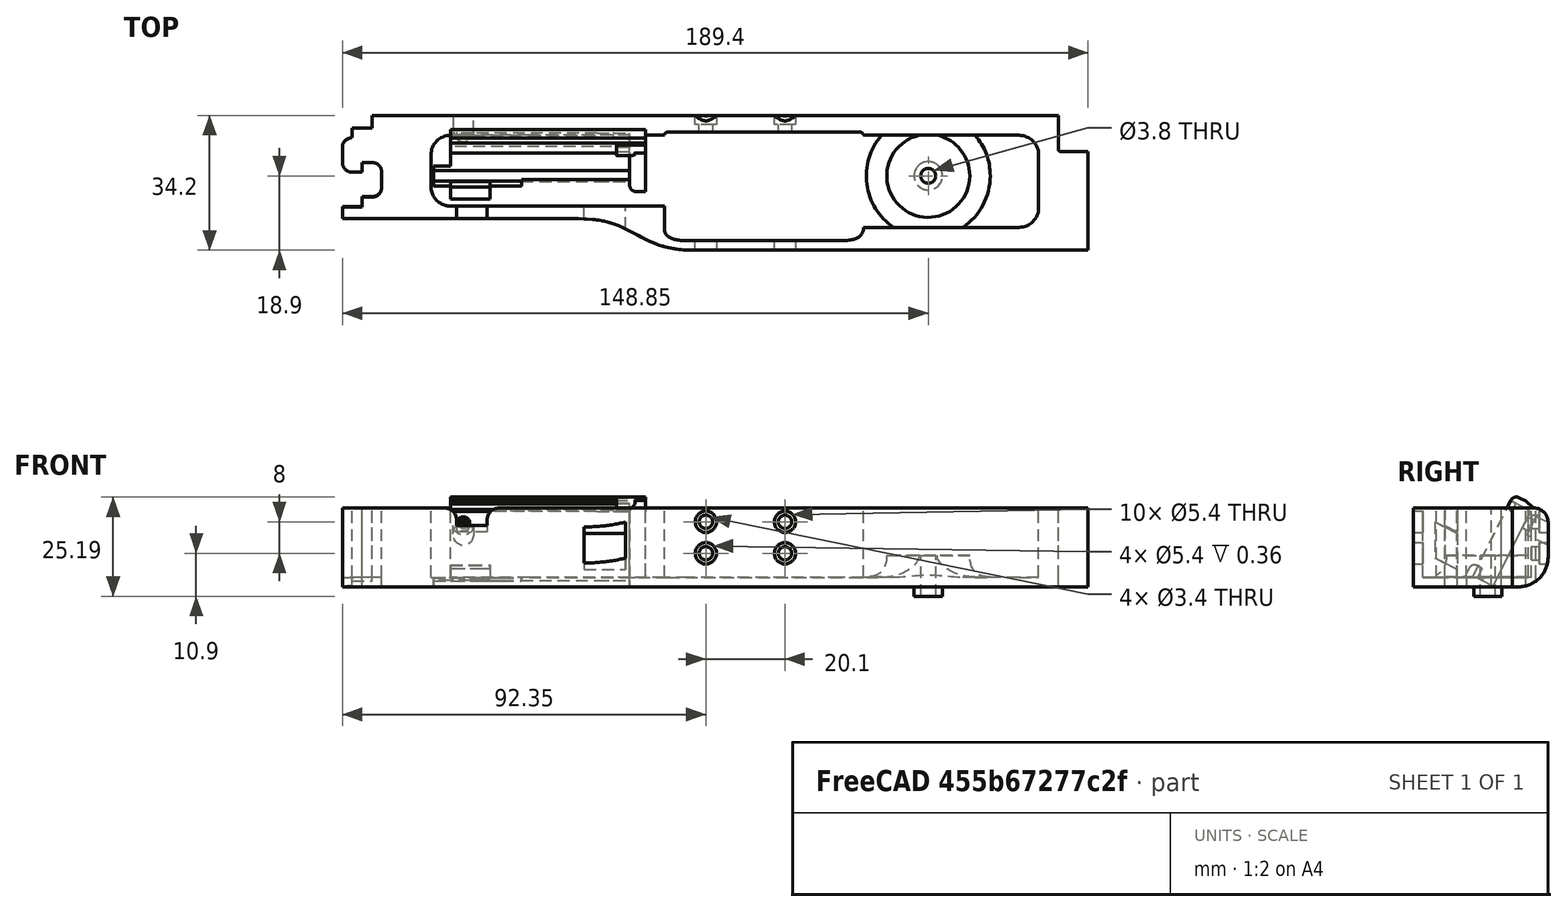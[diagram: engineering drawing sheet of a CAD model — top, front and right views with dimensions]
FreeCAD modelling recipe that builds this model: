
FCSTD DOCUMENT  (FreeCAD 0.19R0.19.2)
Label: v0_992
License: All rights reserved
LicenseURL: http://en.wikipedia.org/wiki/All_rights_reserved
objects: Sketcher::SketchObject×34, Part::Extrusion×28, Part::Cut×14, Part::Fillet×13, Part::MultiFuse×10, Part::Box×8, App::MeasureDistance×4, Part::Revolution×1, Mesh::Feature×1
note: 108 computed .brp shape members not serialized (recipe doc carries the construction recipe); baked Part::Feature solids carry a one-line shape summary decoded from their .brp

FEATURE [Sketcher::SketchObject] Sketch
  FullyConstrained = true
  sketch-geometry (36):
    g0: LineSegment StartX=0 StartY=0 StartZ=0 EndX=154.4 EndY=0 EndZ=0
    g1: LineSegment StartX=154.4 StartY=0 StartZ=0 EndX=154.4 EndY=-7.6 EndZ=0
    g2: LineSegment StartX=32.5209 StartY=-26.2 StartZ=0 EndX=-7.5 EndY=-26.2 EndZ=0
    g3-g7: Circle x5 (B-spline internal-alignment scaffolding for g8; pole/knot coordinates omitted)
    g8: BSplineCurve PolesCount=5 KnotsCount=3 Degree=3 IsPeriodic=0
    g9: GeomPoint X=61.85 Y=-33.8 Z=0
    g10: GeomPoint X=47.185 Y=-29.9 Z=0
    g11: GeomPoint X=32.5209 Y=-26.2 Z=0
    g12: Circle CenterX=121.35 CenterY=-14.3 CenterZ=0 NormalX=0 NormalY=0 NormalZ=1 AngleXU=0 Radius=3.25
    g13: LineSegment StartX=-7.5 StartY=-26.2 StartZ=0 EndX=-27.5 EndY=-26.2 EndZ=0
    g14: LineSegment StartX=-20 StartY=0 StartZ=0 EndX=0 EndY=0 EndZ=0
    g15: LineSegment StartX=-25 StartY=-3.1 StartZ=0 EndX=-20 EndY=-3.1 EndZ=0
    g16: LineSegment StartX=-25 StartY=-3.1 StartZ=0 EndX=-25 EndY=-5.6 EndZ=0
    g17: LineSegment StartX=-27.5 StartY=-8.1 StartZ=0 EndX=-27.5 EndY=-11.85 EndZ=0
    g18: ArcOfCircle CenterX=-25 CenterY=-8.1 CenterZ=0 NormalX=0 NormalY=0 NormalZ=1 AngleXU=0 Radius=2.5 StartAngle=1.5708 EndAngle=3.14159
    g19: LineSegment StartX=-25 StartY=-14.35 StartZ=0 EndX=-22.5 EndY=-14.35 EndZ=0
    g20: ArcOfCircle CenterX=-25 CenterY=-11.85 CenterZ=0 NormalX=0 NormalY=0 NormalZ=1 AngleXU=0 Radius=2.5 StartAngle=3.14159 EndAngle=4.71239
    g21: LineSegment StartX=-22.5 StartY=-14.35 StartZ=0 EndX=-22.5 EndY=-11.85 EndZ=0
    g22: LineSegment StartX=-22.5 StartY=-11.85 StartZ=0 EndX=-20 EndY=-11.85 EndZ=0
    g23: ArcOfCircle CenterX=-20 CenterY=-14.35 CenterZ=0 NormalX=0 NormalY=0 NormalZ=1 AngleXU=0 Radius=2.5 StartAngle=8e-16 EndAngle=1.5708
    g24: LineSegment StartX=-17.5 StartY=-14.35 StartZ=0 EndX=-17.5 EndY=-18.1 EndZ=0
    g25: ArcOfCircle CenterX=-20 CenterY=-18.1 CenterZ=0 NormalX=0 NormalY=0 NormalZ=1 AngleXU=0 Radius=2.5 StartAngle=4.71239 EndAngle=6.28319
    g26: LineSegment StartX=-22.5 StartY=-20.6 StartZ=0 EndX=-20 EndY=-20.6 EndZ=0
    g27: LineSegment StartX=-22.5 StartY=-20.6 StartZ=0 EndX=-22.5 EndY=-23.1 EndZ=0
    g28: LineSegment StartX=-27.5 StartY=-23.1 StartZ=0 EndX=-22.5 EndY=-23.1 EndZ=0
    g29: LineSegment StartX=-20 StartY=-3.1 StartZ=0 EndX=-20 EndY=0 EndZ=0
    g30: LineSegment StartX=-27.5 StartY=-23.1 StartZ=0 EndX=-27.5 EndY=-26.2 EndZ=0
    g31: LineSegment StartX=154.4 StartY=-7.6 StartZ=0 EndX=154.4 EndY=-8.6 EndZ=0
    g32: ArcOfCircle CenterX=154.9 CenterY=-8.6 CenterZ=0 NormalX=0 NormalY=0 NormalZ=1 AngleXU=0 Radius=0.5 StartAngle=3.14159 EndAngle=4.71239
    g33: LineSegment StartX=154.9 StartY=-9.1 StartZ=0 EndX=161.9 EndY=-9.1 EndZ=0
    g34: LineSegment StartX=161.9 StartY=-9.1 StartZ=0 EndX=161.9 EndY=-33.8 EndZ=0
    g35: LineSegment StartX=161.9 StartY=-33.8 StartZ=0 EndX=61.85 EndY=-33.8 EndZ=0
  constraints (72):
    c: PointOnObject(g0,g-2)
    c: Horizontal(g0)
    c: Distance(g0) = 154.4
    c: DistanceY(g-1,g0) = 0
    c: Vertical(g1)
    c: Distance(g1) = 7.6
    c: Coincident(g1,g0)
    c: Horizontal(g2)
    c: Block(g2)
    c: Weight(g3) = 1
    c: Coincident(g8,g2)
    c: InternalAlignment(g3-g7 -> g8) x5
    c: InternalAlignment(g9,g8)
    c: InternalAlignment(g10,g8)
    c: InternalAlignment(g11,g8)
    c: Block(g12)
    c: Coincident(g13,g2)
    c: Horizontal(g13)
    c: Distance(g13) = 20
    c: Horizontal(g14)
    c: Distance(g14) = 20
    c: Coincident(g14,g0)
    c: Horizontal(g15)
    c: Vertical(g16)
    c: Coincident(g16,g15)
    c: Vertical(g17)
    c: Coincident(g18,g16)
    c: Block(g18)
    c: Coincident(g17,g18)
    c: Horizontal(g19)
    c: Coincident(g20,g17)
    c: Block(g20)
    c: Block(g19)
    c: Vertical(g21)
    c: Coincident(g21,g19)
    c: Horizontal(g22)
    c: Coincident(g22,g21)
    c: Coincident(g23,g22)
    c: Vertical(g24)
    c: Block(g23)
    c: Coincident(g24,g23)
    c: Coincident(g25,g24)
    c: Block(g25)
    c: Horizontal(g26)
    c: Coincident(g26,g25)
    c: Vertical(g27)
    c: Coincident(g27,g26)
    c: Horizontal(g28)
    c: Coincident(g28,g27)
    c: Block(g15)
    c: Block(g28)
    c: Coincident(g29,g15)
    c: Coincident(g29,g14)
    c: Vertical(g29)
    c: Coincident(g30,g28)
    c: Coincident(g30,g13)
    c: Vertical(g30)
    c: Vertical(g31)
    c: Distance(g31) = 1
    c: Coincident(g31,g1)
    c: Coincident(g32,g31)
    c: Block(g32)
    c: Coincident(g33,g32)
    c: Horizontal(g33)
    c: Coincident(g34,g33)
    c: Vertical(g34)
    c: Block(g34)
    c: Coincident(g35,g34)
    c: Horizontal(g35)
    c: Block(g35)
    c: Coincident(g8,g35)
    c: Block(g8)
FEATURE [Part::Extrusion] Extrude  label="mainBodyBaseExtrude"
  Base = -> Sketch
  Dir = (0,0,1)
  DirMode = 2
  FaceMakerClass = Part::FaceMakerBullseye
  LengthFwd = 2.4
  LengthRev = 0
  Solid = true
  Symmetric = false
FEATURE [Sketcher::SketchObject] Sketch001
  FullyConstrained = true
  sketch-geometry (75):
    g0: ArcOfCircle CenterX=144.4 CenterY=-10 CenterZ=0 NormalX=0 NormalY=0 NormalZ=1 AngleXU=0 Radius=5 StartAngle=4.345e-13 EndAngle=1.5708
    g1: LineSegment StartX=32.5209 StartY=-26.2 StartZ=0 EndX=-7.49911 EndY=-26.2 EndZ=0
    g2: LineSegment StartX=0 StartY=0 StartZ=0 EndX=154.4 EndY=0 EndZ=0
    g3-g7: Circle x5 (B-spline internal-alignment scaffolding for g8; pole/knot coordinates omitted)
    g8: BSplineCurve PolesCount=5 KnotsCount=3 Degree=3 IsPeriodic=0
    g9: GeomPoint X=61.85 Y=-33.8 Z=0
    g10: GeomPoint X=47.1857 Y=-29.9 Z=0
    g11: GeomPoint X=32.5209 Y=-26.2 Z=0
    g12: LineSegment StartX=154.4 StartY=0 StartZ=0 EndX=154.4 EndY=-7.6 EndZ=0
    g13: LineSegment StartX=20 StartY=-5 StartZ=0 EndX=54.35 EndY=-5 EndZ=0
    g14: LineSegment StartX=104.85 StartY=-5 StartZ=0 EndX=144.4 EndY=-5 EndZ=0
    g15: LineSegment StartX=54.35 StartY=-23 StartZ=0 EndX=20 EndY=-23 EndZ=0
    g16: LineSegment StartX=-27.4991 StartY=-26.2 StartZ=0 EndX=-7.49911 EndY=-26.2 EndZ=0
    g17: LineSegment StartX=-20 StartY=0 StartZ=0 EndX=0 EndY=0 EndZ=0
    g18: LineSegment StartX=-27.4991 StartY=-23.2 StartZ=0 EndX=-22.5 EndY=-23.2 EndZ=0
    g19: LineSegment StartX=-22.5 StartY=-20.7 StartZ=0 EndX=-22.5 EndY=-23.2 EndZ=0
    g20: LineSegment StartX=-22.5 StartY=-20.7 StartZ=0 EndX=-20 EndY=-20.7 EndZ=0
    g21: ArcOfCircle CenterX=-20 CenterY=-18.2 CenterZ=0 NormalX=0 NormalY=0 NormalZ=1 AngleXU=0 Radius=2.5 StartAngle=4.71239 EndAngle=6.28319
    g22: LineSegment StartX=-17.5 StartY=-14.4 StartZ=0 EndX=-17.5 EndY=-18.2 EndZ=0
    g23: ArcOfCircle CenterX=-20 CenterY=-14.4 CenterZ=0 NormalX=0 NormalY=0 NormalZ=1 AngleXU=0 Radius=2.5 StartAngle=9e-16 EndAngle=1.5708
    g24: LineSegment StartX=-22.5 StartY=-11.9 StartZ=0 EndX=-20 EndY=-11.9 EndZ=0
    g25: LineSegment StartX=-22.5 StartY=-14.4 StartZ=0 EndX=-22.5 EndY=-11.9 EndZ=0
    g26: LineSegment StartX=-25 StartY=-14.4 StartZ=0 EndX=-22.5 EndY=-14.4 EndZ=0
    g27: ArcOfCircle CenterX=-25 CenterY=-11.9 CenterZ=0 NormalX=0 NormalY=0 NormalZ=1 AngleXU=0 Radius=2.5 StartAngle=3.14159 EndAngle=4.71239
    g28: LineSegment StartX=-27.5 StartY=-8.1 StartZ=0 EndX=-27.5 EndY=-11.9 EndZ=0
    g29: ArcOfCircle CenterX=-25 CenterY=-8.1 CenterZ=0 NormalX=0 NormalY=0 NormalZ=1 AngleXU=0 Radius=2.5 StartAngle=1.5708 EndAngle=3.14159
    g30: LineSegment StartX=-25 StartY=-3.1 StartZ=0 EndX=-25 EndY=-5.6 EndZ=0
    g31: LineSegment StartX=-20 StartY=-3.1 StartZ=0 EndX=-25 EndY=-3.1 EndZ=0
    g32: LineSegment StartX=-20 StartY=0 StartZ=0 EndX=-20 EndY=-3.1 EndZ=0
    g33: LineSegment StartX=-27.4991 StartY=-26.2 StartZ=0 EndX=-27.4991 EndY=-23.2 EndZ=0
    g34: LineSegment StartX=4.09e-14 StartY=-5 StartZ=0 EndX=20 EndY=-5 EndZ=0
    g35: ArcOfCircle CenterX=7.1e-15 CenterY=-18 CenterZ=0 NormalX=0 NormalY=0 NormalZ=1 AngleXU=0 Radius=5 StartAngle=3.14159 EndAngle=4.71239
    g36: ArcOfCircle CenterX=4.26e-14 CenterY=-10 CenterZ=0 NormalX=0 NormalY=0 NormalZ=1 AngleXU=0 Radius=5 StartAngle=1.5708 EndAngle=3.14159
    g37: LineSegment StartX=-5 StartY=-18 StartZ=0 EndX=-5 EndY=-10 EndZ=0
    g38: LineSegment StartX=6.2e-15 StartY=-23 StartZ=0 EndX=20 EndY=-23 EndZ=0
    g39: LineSegment StartX=154.4 StartY=-7.6 StartZ=0 EndX=154.4 EndY=-8.6 EndZ=0
    g40: LineSegment StartX=154.9 StartY=-9.1 StartZ=0 EndX=161.9 EndY=-9.1 EndZ=0
    g41: ArcOfCircle CenterX=154.9 CenterY=-8.6 CenterZ=0 NormalX=0 NormalY=0 NormalZ=1 AngleXU=0 Radius=0.5 StartAngle=3.14159 EndAngle=4.71299
    g42: LineSegment StartX=104.85 StartY=-28.3916 StartZ=0 EndX=144.408 EndY=-28.3916 EndZ=0
    g43: LineSegment StartX=149.4 StartY=-10 StartZ=0 EndX=149.4 EndY=-23.4 EndZ=0
    g44: ArcOfCircle CenterX=144.408 CenterY=-23.4 CenterZ=0 NormalX=0 NormalY=0 NormalZ=1 AngleXU=0 Radius=4.99164 StartAngle=4.71239 EndAngle=6.28319
    g45: LineSegment StartX=104.85 StartY=-28.3916 StartZ=0 EndX=104.85 EndY=-28.7833 EndZ=0
    g46: LineSegment StartX=54.35 StartY=-28.7916 StartZ=0 EndX=54.35 EndY=-23 EndZ=0
    g47: LineSegment StartX=161.9 StartY=-33.8 StartZ=0 EndX=161.9 EndY=-9.1 EndZ=0
    g48: LineSegment StartX=61.85 StartY=-33.8 StartZ=0 EndX=161.9 EndY=-33.8 EndZ=0
    g49: Circle CenterX=54.35 CenterY=-28.7916 CenterZ=0 NormalX=0 NormalY=0 NormalZ=1 AngleXU=0 Radius=1
    g50: Circle CenterX=54.35 CenterY=-31.7916 CenterZ=0 NormalX=0 NormalY=0 NormalZ=1 AngleXU=0 Radius=1
    g51: Circle CenterX=57.35 CenterY=-31.7916 CenterZ=0 NormalX=0 NormalY=0 NormalZ=1 AngleXU=0 Radius=1
    g52: BSplineCurve PolesCount=3 KnotsCount=2 Degree=2 IsPeriodic=0
    g53: GeomPoint X=54.35 Y=-28.7916 Z=0
    g54: GeomPoint X=57.35 Y=-31.7916 Z=0
    g55: Circle CenterX=104.85 CenterY=-28.7833 CenterZ=0 NormalX=0 NormalY=0 NormalZ=1 AngleXU=0 Radius=1
    g56: Circle CenterX=104.85 CenterY=-31.7916 CenterZ=0 NormalX=0 NormalY=0 NormalZ=1 AngleXU=0 Radius=1
    g57: Circle CenterX=101.85 CenterY=-31.7916 CenterZ=0 NormalX=0 NormalY=0 NormalZ=1 AngleXU=0 Radius=1
    g58: BSplineCurve PolesCount=3 KnotsCount=2 Degree=2 IsPeriodic=0
    g59: GeomPoint X=104.85 Y=-28.7833 Z=0
    g60: GeomPoint X=101.85 Y=-31.7916 Z=0
    g61: LineSegment StartX=57.35 StartY=-31.7916 StartZ=0 EndX=101.85 EndY=-31.7916 EndZ=0
    g62: Circle CenterX=54.35 CenterY=-5 CenterZ=0 NormalX=0 NormalY=0 NormalZ=1 AngleXU=0 Radius=1
    g63: Circle CenterX=54.35 CenterY=-4 CenterZ=0 NormalX=0 NormalY=0 NormalZ=1 AngleXU=0 Radius=1
    g64: Circle CenterX=55.15 CenterY=-4 CenterZ=0 NormalX=0 NormalY=0 NormalZ=1 AngleXU=0 Radius=1
    g65: BSplineCurve PolesCount=3 KnotsCount=2 Degree=2 IsPeriodic=0
    g66: GeomPoint X=54.35 Y=-5 Z=0
    g67: GeomPoint X=55.15 Y=-4 Z=0
    g68: Circle CenterX=104.85 CenterY=-5 CenterZ=0 NormalX=0 NormalY=0 NormalZ=1 AngleXU=0 Radius=1
    g69: Circle CenterX=104.85 CenterY=-4 CenterZ=0 NormalX=0 NormalY=0 NormalZ=1 AngleXU=0 Radius=1
    g70: Circle CenterX=104.05 CenterY=-4 CenterZ=0 NormalX=0 NormalY=0 NormalZ=1 AngleXU=0 Radius=1
    g71: BSplineCurve PolesCount=3 KnotsCount=2 Degree=2 IsPeriodic=0
    g72: GeomPoint X=104.85 Y=-5 Z=0
    g73: GeomPoint X=104.05 Y=-4 Z=0
    g74: LineSegment StartX=104.05 StartY=-4 StartZ=0 EndX=55.15 EndY=-4 EndZ=0
  constraints (156):
    c: PointOnObject(g2,g-2)
    c: DistanceY(g-1,g2) = 0
    c: Block(g0)
    c: Horizontal(g1)
    c: Distance(g1) = 40.02
    c: Horizontal(g2)
    c: Block(g2)
    c: Weight(g3) = 1
    c: Equal(g3, g4-g7) x4
    c: Coincident(g8,g1)
    c: InternalAlignment(g3-g7 -> g8) x5
    c: InternalAlignment(g9,g8)
    c: InternalAlignment(g10,g8)
    c: InternalAlignment(g11,g8)
    c: Vertical(g12)
    c: Coincident(g12,g2)
    c: Distance(g12) = 7.6
    c: Block(g12)
    c: Horizontal(g13)
    c: Coincident(g14,g0)
    c: Horizontal(g14)
    c: Horizontal(g15)
    c: Horizontal(g16)
    c: Distance(g16) = 20
    c: Coincident(g1,g16)
    c: Horizontal(g17)
    c: Distance(g17) = 20
    c: Coincident(g17,g2)
    c: Horizontal(g31)
    c: Vertical(g30)
    c: Coincident(g29,g30)
    c: Vertical(g28)
    c: Block(g29)
    c: Coincident(g27,g28)
    c: Block(g27)
    c: Horizontal(g26)
    c: Coincident(g26,g27)
    c: Vertical(g25)
    c: Coincident(g25,g26)
    c: Horizontal(g24)
    c: Coincident(g23,g24)
    c: Block(g23)
    c: Vertical(g22)
    c: Coincident(g21,g22)
    c: Block(g21)
    c: Horizontal(g20)
    c: Coincident(g20,g21)
    c: Vertical(g19)
    c: Coincident(g19,g20)
    c: Horizontal(g18)
    c: Coincident(g18,g19)
    c: Coincident(g32,g17)
    c: Coincident(g32,g31)
    c: Vertical(g32)
    c: Coincident(g33,g16)
    c: Coincident(g33,g18)
    c: Vertical(g33)
    c: Block(g33)
    c: Block(g18)
    c: Block(g22)
    c: Block(g26)
    c: Block(g25)
    c: Block(g24)
    c: Block(g28)
    c: Block(g31)
    c: Block(g30)
    c: Horizontal(g34)
    c: Distance(g34) = 20
    c: Block(g35)
    c: Block(g36)
    c: Coincident(g37,g35)
    c: Coincident(g37,g36)
    c: Vertical(g37)
    c: Coincident(g38,g35)
    c: Coincident(g38,g15)
    c: Horizontal(g38)
    c: Block(g38)
    c: Block(g34)
    c: Block(g13)
    c: Vertical(g39)
    c: Distance(g39) = 1
    c: Coincident(g39,g12)
    c: Horizontal(g40)
    c: Coincident(g41,g39)
    c: Coincident(g41,g40)
    c: Block(g39)
    c: Block(g41)
    c: Horizontal(g42)
    c: Vertical(g43)
    c: Distance(g43) = 13.4
    c: Coincident(g43,g0)
    c: Block(g42)
    c: Block(g43)
    c: Coincident(g44,g43)
    c: Coincident(g44,g42)
    c: Block(g44)
    c: Distance(g15) = 34.35
    c: Coincident(g45,g42)
    c: Vertical(g45)
    c: Coincident(g46,g15)
    c: Vertical(g46)
    c: Coincident(g47,g40)
    c: Vertical(g47)
    c: Block(g47)
    c: Coincident(g48,g47)
    c: Horizontal(g48)
    c: Block(g48)
    c: Coincident(g8,g48)
    c: Block(g8)
    c: Coincident(g52,g46)
    c: Weight(g49) = 1
    c: Equal(g49,g50)
    c: Equal(g49,g51)
    c: InternalAlignment(g49,g52)
    c: InternalAlignment(g50,g52)
    c: InternalAlignment(g51,g52)
    c: InternalAlignment(g53,g52)
    c: InternalAlignment(g54,g52)
    c: Coincident(g58,g45)
    c: Weight(g55) = 1
    c: Equal(g55,g56)
    c: Equal(g55,g57)
    c: InternalAlignment(g55,g58)
    c: InternalAlignment(g56,g58)
    c: InternalAlignment(g57,g58)
    c: InternalAlignment(g59,g58)
    c: InternalAlignment(g60,g58)
    c: Block(g58)
    c: Block(g52)
    c: Coincident(g61,g52)
    c: Coincident(g61,g58)
    c: Horizontal(g61)
    c: Block(g14)
    c: Coincident(g65,g13)
    c: Weight(g62) = 1
    c: Equal(g62,g63)
    c: Equal(g62,g64)
    c: InternalAlignment(g62,g65)
    c: InternalAlignment(g63,g65)
    c: InternalAlignment(g64,g65)
    c: InternalAlignment(g66,g65)
    c: InternalAlignment(g67,g65)
    c: Block(g65)
    c: Coincident(g71,g14)
    c: Weight(g68) = 1
    c: Equal(g68,g69)
    c: Equal(g68,g70)
    c: InternalAlignment(g68,g71)
    c: InternalAlignment(g69,g71)
    c: InternalAlignment(g70,g71)
    c: InternalAlignment(g72,g71)
    c: InternalAlignment(g73,g71)
    c: Block(g71)
    c: Coincident(g74,g71)
    c: Coincident(g74,g65)
    c: Horizontal(g74)
FEATURE [Sketcher::SketchObject] Sketch005
  FullyConstrained = true
  Placement = pos=(0,0,0) rot=(1,0,0;1.5708rad)
  sketch-geometry (4):
    g0: Circle CenterX=84.95 CenterY=16.5 CenterZ=0 NormalX=0 NormalY=0 NormalZ=1 AngleXU=0 Radius=1.7
    g1: Circle CenterX=84.95 CenterY=8.5 CenterZ=0 NormalX=0 NormalY=0 NormalZ=1 AngleXU=0 Radius=1.7
    g2: Circle CenterX=64.85 CenterY=8.5 CenterZ=0 NormalX=0 NormalY=0 NormalZ=1 AngleXU=0 Radius=1.7
    g3: Circle CenterX=64.85 CenterY=16.5 CenterZ=0 NormalX=0 NormalY=0 NormalZ=1 AngleXU=0 Radius=1.7
  constraints (4):
    c: Block(g0)
    c: Block(g1)
    c: Block(g2)
    c: Block(g3)
FEATURE [Part::Extrusion] Extrude004  label="removeFromMainBodyToCreateScrewHolesForSolenoidExtrude004"
  Base = -> Sketch005
  Dir = (0,-1,1.1e-15)
  DirMode = 2
  FaceMakerClass = Part::FaceMakerBullseye
  LengthFwd = 10
  LengthRev = 0
  Solid = true
  Symmetric = false
FEATURE [Sketcher::SketchObject] Sketch004
  FullyConstrained = true
  Placement = pos=(0,0,0) rot=(1,0,0;1.5708rad)
  sketch-geometry (12):
    g0: LineSegment StartX=15.75 StartY=2.5 StartZ=0 EndX=15.75 EndY=0 EndZ=0
    g1: Circle CenterX=15.75 CenterY=2.5 CenterZ=0 NormalX=0 NormalY=0 NormalZ=1 AngleXU=0 Radius=1
    g2: Circle CenterX=10.55 CenterY=2.5 CenterZ=0 NormalX=0 NormalY=0 NormalZ=1 AngleXU=0 Radius=1
    g3: Circle CenterX=10.55 CenterY=8 CenterZ=0 NormalX=0 NormalY=0 NormalZ=1 AngleXU=0 Radius=1
    g4: BSplineCurve PolesCount=3 KnotsCount=2 Degree=2 IsPeriodic=0
    g5: GeomPoint X=15.75 Y=2.5 Z=0
    g6: GeomPoint X=10.55 Y=8 Z=0
    g7: LineSegment StartX=1.9 StartY=8 StartZ=0 EndX=10.55 EndY=8 EndZ=0
    g8: LineSegment StartX=1.9 StartY=-2.4 StartZ=0 EndX=1.9 EndY=8 EndZ=0
    g9: LineSegment StartX=3.30092 StartY=-2.4 StartZ=0 EndX=3.30092 EndY=0 EndZ=0
    g10: LineSegment StartX=15.75 StartY=0 StartZ=0 EndX=3.30092 EndY=0 EndZ=0
    g11: LineSegment StartX=3.30092 StartY=-2.4 StartZ=0 EndX=1.9 EndY=-2.4 EndZ=0
  constraints (26):
    c: Vertical(g0)
    c: Distance(g0) = 2.5
    c: Coincident(g4,g0)
    c: Weight(g1) = 1
    c: Equal(g1,g2)
    c: Equal(g1,g3)
    c: InternalAlignment(g1,g4)
    c: InternalAlignment(g2,g4)
    c: InternalAlignment(g3,g4)
    c: InternalAlignment(g5,g4)
    c: InternalAlignment(g6,g4)
    c: Block(g4)
    c: Coincident(g7,g4)
    c: Horizontal(g7)
    c: Vertical(g8)
    c: Coincident(g8,g7)
    c: Block(g8)
    c: Vertical(g9)
    c: Coincident(g10,g0)
    c: PointOnObject(g10,g-1)
    c: Horizontal(g10)
    c: Coincident(g10,g9)
    c: Block(g9)
    c: Coincident(g11,g9)
    c: Coincident(g11,g8)
    c: Horizontal(g11)
FEATURE [Sketcher::SketchObject] Sketch007
  FullyConstrained = true
  Placement = pos=(0,-14.3,2.37) rot=(-1,0,0;2.03453rad)
  sketch-geometry (6):
    g0: LineSegment StartX=0 StartY=0 StartZ=0 EndX=45.5 EndY=0 EndZ=0
    g1: LineSegment StartX=0 StartY=0 StartZ=0 EndX=0 EndY=-21.2 EndZ=0
    g2: LineSegment StartX=45.5 StartY=0 StartZ=0 EndX=49.5 EndY=0 EndZ=0
    g3: LineSegment StartX=49.5 StartY=0 StartZ=0 EndX=49.5 EndY=-21.2 EndZ=0
    g4: LineSegment StartX=49.5 StartY=-21.2 StartZ=0 EndX=0 EndY=-21.2 EndZ=0
    g5: Circle CenterX=3.25 CenterY=-18.05 CenterZ=0 NormalX=0 NormalY=0 NormalZ=1 AngleXU=0 Radius=1.6
  constraints (15):
    c: Coincident(g0,g-1)
    c: Horizontal(g0)
    c: Distance(g0) = 45.5
    c: Coincident(g1,g0)
    c: Vertical(g1)
    c: Horizontal(g2)
    c: Distance(g2) = 4
    c: Coincident(g2,g0)
    c: Coincident(g3,g2)
    c: Vertical(g3)
    c: Block(g3)
    c: Coincident(g4,g3)
    c: Horizontal(g4)
    c: Coincident(g4,g1)
    c: Block(g5)
FEATURE [Part::Extrusion] Extrude005  label="solenoidDriverHolderExtrude005"
  Base = -> Sketch007
  Dir = (0,0.894389,-0.447291)
  DirMode = 2
  FaceMakerClass = Part::FaceMakerBullseye
  LengthFwd = 10
  LengthRev = 0
  Placement = pos=(0,0,-2) rot=(0,0,1;0rad)
  Solid = true
  Symmetric = false
FEATURE [Sketcher::SketchObject] Sketch008
  FullyConstrained = false
  Placement = pos=(0,-4.3,-2.6) rot=(-1,0,0;2.03453rad)
  sketch-geometry (1):
    g0: Circle CenterX=42.25 CenterY=-3.15 CenterZ=0 NormalX=0 NormalY=0 NormalZ=1 AngleXU=0 Radius=4.5
FEATURE [Sketcher::SketchObject] Sketch009
  FullyConstrained = true
  Placement = pos=(0,-4.3,-2.6) rot=(-1,0,0;2.03453rad)
  sketch-geometry (1):
    g0: Circle CenterX=3.25 CenterY=-18.0217 CenterZ=0 NormalX=0 NormalY=0 NormalZ=1 AngleXU=0 Radius=2.6
  constraints (1):
    c: Block(g0)
FEATURE [Sketcher::SketchObject] Sketch010
  FullyConstrained = true
  Placement = pos=(0,-14.3,2.37) rot=(-1,0,0;2.03453rad)
  sketch-geometry (1):
    g0: Circle CenterX=3.25 CenterY=-18.05 CenterZ=0 NormalX=0 NormalY=0 NormalZ=1 AngleXU=0 Radius=1.6
  constraints (1):
    c: Block(g0)
FEATURE [Part::Extrusion] Extrude008  label="removeFromScrewHole3"
  Base = -> Sketch010
  Dir = (0,0.894389,-0.447291)
  DirMode = 2
  FaceMakerClass = Part::FaceMakerBullseye
  LengthFwd = -25
  LengthRev = 0
  Placement = pos=(0,4,-4) rot=(0,0,1;0rad)
  Solid = true
  Symmetric = false
FEATURE [Sketcher::SketchObject] Sketch011
  FullyConstrained = true
  Placement = pos=(0,-14.3,2.37) rot=(-1,0,0;2.03453rad)
  sketch-geometry (4):
    g0: LineSegment StartX=49.5 StartY=-21.2 StartZ=0 EndX=49.5 EndY=-22.8 EndZ=0
    g1: LineSegment StartX=49.5 StartY=-22.8 StartZ=0 EndX=0.002238 EndY=-22.8 EndZ=0
    g2: LineSegment StartX=0.002238 StartY=-21.2 StartZ=0 EndX=0.002238 EndY=-22.8 EndZ=0
    g3: LineSegment StartX=49.5 StartY=-21.2 StartZ=0 EndX=0.002238 EndY=-21.2 EndZ=0
  constraints (10):
    c: Vertical(g0)
    c: Distance(g0) = 1.6
    c: Coincident(g1,g0)
    c: Horizontal(g1)
    c: Vertical(g2)
    c: Coincident(g2,g1)
    c: Coincident(g3,g0)
    c: Coincident(g3,g2)
    c: Horizontal(g3)
    c: Block(g3)
FEATURE [Part::Extrusion] Extrude009  label="solenoidDriverTopLipFront"
  Base = -> Sketch011
  Dir = (0,0.894389,-0.447291)
  DirMode = 2
  FaceMakerClass = Part::FaceMakerBullseye
  LengthFwd = -2
  LengthRev = 0
  Placement = pos=(0,-2.9,-0.35) rot=(0,0,1;0rad)
  Solid = true
  Symmetric = false
FEATURE [Sketcher::SketchObject] Sketch012
  FullyConstrained = true
  Placement = pos=(0,-14.3,2.37) rot=(-1,0,0;2.03453rad)
  sketch-geometry (4):
    g0: LineSegment StartX=49.5 StartY=-21.2 StartZ=0 EndX=49.5 EndY=-22.8 EndZ=0
    g1: LineSegment StartX=49.5 StartY=-22.8 StartZ=0 EndX=0.002238 EndY=-22.8 EndZ=0
    g2: LineSegment StartX=0.002238 StartY=-21.2 StartZ=0 EndX=0.002238 EndY=-22.8 EndZ=0
    g3: LineSegment StartX=49.5 StartY=-21.2 StartZ=0 EndX=0.002238 EndY=-21.2 EndZ=0
  constraints (10):
    c: Vertical(g0)
    c: Distance(g0) = 1.6
    c: Coincident(g1,g0)
    c: Horizontal(g1)
    c: Vertical(g2)
    c: Coincident(g2,g1)
    c: Coincident(g3,g0)
    c: Coincident(g3,g2)
    c: Horizontal(g3)
    c: Block(g3)
FEATURE [Part::Extrusion] Extrude010  label="solenoidDriverTopLipLowerExtrude010"
  Base = -> Sketch012
  Dir = (0,0.894389,-0.447291)
  DirMode = 2
  FaceMakerClass = Part::FaceMakerBullseye
  LengthFwd = 5.05
  LengthRev = 0
  Solid = true
  Symmetric = false
FEATURE [Sketcher::SketchObject] Sketch015
  FullyConstrained = true
  Placement = pos=(0,-14.3,2.37) rot=(-1,0,0;2.03453rad)
  sketch-geometry (4):
    g0: LineSegment StartX=0 StartY=1.5 StartZ=0 EndX=0 EndY=0 EndZ=0
    g1: LineSegment StartX=0 StartY=1.5 StartZ=0 EndX=5 EndY=1.5 EndZ=0
    g2: LineSegment StartX=5 StartY=1.5 StartZ=0 EndX=5 EndY=0 EndZ=0
    g3: LineSegment StartX=0 StartY=0 StartZ=0 EndX=5 EndY=0 EndZ=0
  constraints (13):
    c: Vertical(g0)
    c: Distance(g0) = 1.5
    c: Horizontal(g1)
    c: Distance(g1) = 5
    c: Coincident(g1,g0)
    c: Vertical(g2)
    c: Distance(g2) = 1.5
    c: Coincident(g2,g1)
    c: Block(g1)
    c: Block(g2)
    c: Block(g0)
    c: Coincident(g3,g0)
    c: Coincident(g3,g2)
FEATURE [Part::Extrusion] Extrude013  label="solenoidDriverBottomLipTopExtrude012"
  Base = -> Sketch015
  Dir = (0,0.894389,-0.447291)
  DirMode = 2
  FaceMakerClass = Part::FaceMakerBullseye
  LengthFwd = -6.5
  LengthRev = 0
  Placement = pos=(0,-14.15,19.65) rot=(1,0,0;1.5708rad)
  Solid = true
  Symmetric = false
FEATURE [Sketcher::SketchObject] Sketch016
  FullyConstrained = true
  Placement = pos=(0,0,0) rot=(1,0,0;1.5708rad)
  sketch-geometry (4):
    g0: Circle CenterX=84.15 CenterY=16.5 CenterZ=0 NormalX=0 NormalY=0 NormalZ=1 AngleXU=0 Radius=2.7
    g1: Circle CenterX=64.05 CenterY=16.5 CenterZ=0 NormalX=0 NormalY=0 NormalZ=1 AngleXU=0 Radius=2.7
    g2: Circle CenterX=64.05 CenterY=8.5 CenterZ=0 NormalX=0 NormalY=0 NormalZ=1 AngleXU=0 Radius=2.7
    g3: Circle CenterX=84.15 CenterY=8.5 CenterZ=0 NormalX=0 NormalY=0 NormalZ=1 AngleXU=0 Radius=2.7
  constraints (4):
    c: Block(g0)
    c: Block(g1)
    c: Block(g3)
    c: Block(g2)
FEATURE [Part::Extrusion] Extrude014  label="removeFromMainBodyToCreateScrewHoleCounterSinks"
  Base = -> Sketch016
  Dir = (0,-1,1.1e-15)
  DirMode = 2
  FaceMakerClass = Part::FaceMakerBullseye
  LengthFwd = 1.9
  LengthRev = 0
  Placement = pos=(0.8,-0.36,0) rot=(0,0,1;0rad)
  Solid = true
  Symmetric = false
FEATURE [Part::Extrusion] Extrude015  label="removeFromScrewHole2Extrude007"
  Base = -> Sketch009
  Dir = (0,0.894389,-0.447291)
  DirMode = 2
  FaceMakerClass = Part::FaceMakerBullseye
  LengthFwd = 10
  LengthRev = 0
  Placement = pos=(0,-8,2) rot=(0,0,1;0rad)
  Solid = true
  Symmetric = false
FEATURE [Sketcher::SketchObject] Sketch017
  FullyConstrained = true
  Placement = pos=(0,-14.3,2.37) rot=(-1,0,0;2.03453rad)
  sketch-geometry (4):
    g0: LineSegment StartX=0 StartY=1.5 StartZ=0 EndX=0 EndY=0 EndZ=0
    g1: LineSegment StartX=0 StartY=1.5 StartZ=0 EndX=5 EndY=1.5 EndZ=0
    g2: LineSegment StartX=5 StartY=1.5 StartZ=0 EndX=5 EndY=0 EndZ=0
    g3: LineSegment StartX=0 StartY=0 StartZ=0 EndX=5 EndY=0 EndZ=0
  constraints (13):
    c: Vertical(g0)
    c: Distance(g0) = 1.5
    c: Horizontal(g1)
    c: Distance(g1) = 5
    c: Coincident(g1,g0)
    c: Vertical(g2)
    c: Distance(g2) = 1.5
    c: Coincident(g2,g1)
    c: Block(g1)
    c: Block(g2)
    c: Block(g0)
    c: Coincident(g3,g0)
    c: Coincident(g3,g2)
FEATURE [Part::Extrusion] Extrude016  label="solenoidDriverBottomLipTopExtrude013"
  Base = -> Sketch017
  Dir = (0,0.894389,-0.447291)
  DirMode = 2
  FaceMakerClass = Part::FaceMakerBullseye
  LengthFwd = -6.5
  LengthRev = 0
  Placement = pos=(0,-15.45,20.3) rot=(1,0,0;1.5708rad)
  Solid = true
  Symmetric = false
FEATURE [Part::Fillet] Fillet005  label="solenoidDriverBottomLipTopFillet005"
  Base = -> Extrude016
  Edges = 1 edges r=1.4: [Edge6]
FEATURE [Sketcher::SketchObject] Sketch018
  FullyConstrained = true
  Placement = pos=(38.5,-14.3,2.37) rot=(-1,0,0;2.03453rad)
  sketch-geometry (4):
    g0: LineSegment StartX=11 StartY=0 StartZ=0 EndX=11 EndY=1.5 EndZ=0
    g1: LineSegment StartX=11 StartY=0 StartZ=0 EndX=3.6 EndY=0 EndZ=0
    g2: LineSegment StartX=3.6 StartY=0 StartZ=0 EndX=3.6 EndY=1.5 EndZ=0
    g3: LineSegment StartX=11 StartY=1.5 StartZ=0 EndX=3.6 EndY=1.5 EndZ=0
  constraints (12):
    c: PointOnObject(g0,g-1)
    c: Vertical(g0)
    c: Distance(g0) = 1.5
    c: Horizontal(g1)
    c: Distance(g1) = 7.4
    c: Coincident(g1,g0)
    c: Block(g0)
    c: Coincident(g2,g1)
    c: Vertical(g2)
    c: Coincident(g3,g0)
    c: Horizontal(g3)
    c: Coincident(g2,g3)
FEATURE [Part::Extrusion] Extrude017
  Base = -> Sketch018
  Dir = (0,0.894389,-0.447291)
  DirMode = 2
  FaceMakerClass = Part::FaceMakerBullseye
  LengthFwd = 4
  LengthRev = 0
  Placement = pos=(0,-8.212,34.025) rot=(1,0,0;1.5708rad)
  Solid = true
  Symmetric = false
FEATURE [Sketcher::SketchObject] Sketch019
  FullyConstrained = true
  Placement = pos=(0,0,0) rot=(1,0,0;1.5708rad)
  sketch-geometry (4):
    g0: Circle CenterX=84.95 CenterY=8.5 CenterZ=0 NormalX=0 NormalY=0 NormalZ=1 AngleXU=0 Radius=2.7
    g1: Circle CenterX=64.85 CenterY=8.5 CenterZ=0 NormalX=0 NormalY=0 NormalZ=1 AngleXU=0 Radius=2.7
    g2: Circle CenterX=64.85 CenterY=16.5 CenterZ=0 NormalX=0 NormalY=0 NormalZ=1 AngleXU=0 Radius=2.7
    g3: Circle CenterX=84.95 CenterY=16.5 CenterZ=0 NormalX=0 NormalY=0 NormalZ=1 AngleXU=0 Radius=2.7
  constraints (4):
    c: Block(g3)
    c: Block(g2)
    c: Block(g0)
    c: Block(g1)
FEATURE [Part::Extrusion] Extrude019  label="removeSolenoidAdjusterHoles"
  Base = -> Sketch019
  Dir = (0,-1,1.1e-15)
  DirMode = 2
  FaceMakerClass = Part::FaceMakerBullseye
  LengthFwd = 6
  LengthRev = 0
  Placement = pos=(0,-30,0) rot=(0,0,1;0rad)
  Solid = true
  Symmetric = false
FEATURE [Sketcher::SketchObject] Sketch020
  FullyConstrained = true
  Placement = pos=(0,-14.3,2.37) rot=(-1,0,0;2.03453rad)
  sketch-geometry (6):
    g0: LineSegment StartX=45.5 StartY=-21.2 StartZ=0 EndX=49.5 EndY=-21.2 EndZ=0
    g1: LineSegment StartX=45.5 StartY=0 StartZ=0 EndX=49.5 EndY=0 EndZ=0
    g2: LineSegment StartX=49.5 StartY=0 StartZ=0 EndX=49.5 EndY=-21.2 EndZ=0
    g3: LineSegment StartX=4 StartY=0 StartZ=0 EndX=4 EndY=-21.2 EndZ=0
    g4: LineSegment StartX=45.5 StartY=-21.2 StartZ=0 EndX=4 EndY=-21.2 EndZ=0
    g5: LineSegment StartX=4 StartY=0 StartZ=0 EndX=45.5 EndY=0 EndZ=0
  constraints (16):
    c: Horizontal(g0)
    c: Distance(g0) = 4
    c: Horizontal(g1)
    c: Distance(g1) = 4
    c: Coincident(g2,g1)
    c: Coincident(g2,g0)
    c: Vertical(g2)
    c: Block(g2)
    c: Vertical(g3)
    c: Coincident(g4,g0)
    c: Horizontal(g4)
    c: Coincident(g4,g3)
    c: Coincident(g5,g1)
    c: Horizontal(g5)
    c: Block(g3)
    c: Block(g5)
FEATURE [Part::Box] Box  label="Cube"
  AttacherType = Attacher::AttachEngine3D
  Height = 10
  Length = 190
  Placement = pos=(-30,0,0) rot=(0,0,1;0rad)
  Width = 10
FEATURE [Part::Fillet] Fillet008
  Base = -> Box
  Edges = 1 edges r=7.5: [Edge11]
FEATURE [Part::Box] Box001  label="Cube001"
  AttacherType = Attacher::AttachEngine3D
  Height = 10
  Length = 190
  Placement = pos=(-35,0,0) rot=(0,0,1;0rad)
  Width = 10
FEATURE [Part::Cut] Cut  label="filletMain"
  Base = -> Box001
  Placement = pos=(0,-10,0) rot=(0,0,1;0rad)
  Tool = -> Fillet008
FEATURE [Part::Box] Box002  label="Cube002"
  AttacherType = Attacher::AttachEngine3D
  Height = 30
  Length = 190
  Placement = pos=(-20,0,0) rot=(0,0,1;0rad)
  Width = 10
FEATURE [Part::Box] Box003  label="Cube003"
  AttacherType = Attacher::AttachEngine3D
  Height = 10
  Length = 190
  Placement = pos=(-90,-50,-10) rot=(0,0,1;0rad)
  Width = 50
FEATURE [Sketcher::SketchObject] Sketch021
  FullyConstrained = true
  Placement = pos=(0,-14.3,2.37) rot=(-1,0,0;2.03453rad)
  sketch-geometry (6):
    g0: LineSegment StartX=41.65 StartY=-3.15 StartZ=0 EndX=38.95 EndY=-3.15 EndZ=0
    g1: LineSegment StartX=36.25 StartY=-3.15 StartZ=0 EndX=38.95 EndY=-3.15 EndZ=0
    g2: LineSegment StartX=41.65 StartY=-3.15 StartZ=0 EndX=41.65 EndY=-7.15 EndZ=0
    g3: LineSegment StartX=38.95 StartY=-7.15 StartZ=0 EndX=41.65 EndY=-7.15 EndZ=0
    g4: LineSegment StartX=38.95 StartY=-7.15 StartZ=0 EndX=36.25 EndY=-7.15 EndZ=0
    g5: LineSegment StartX=36.25 StartY=-3.15 StartZ=0 EndX=36.25 EndY=-7.15 EndZ=0
  constraints (16):
    c: Horizontal(g0)
    c: Distance(g0) = 2.7
    c: Horizontal(g1)
    c: Distance(g1) = 2.7
    c: Coincident(g1,g0)
    c: Block(g0)
    c: Coincident(g2,g0)
    c: Vertical(g2)
    c: Horizontal(g3)
    c: Coincident(g3,g2)
    c: Horizontal(g4)
    c: Coincident(g5,g1)
    c: Vertical(g5)
    c: Coincident(g5,g4)
    c: Block(g3)
    c: Block(g4)
FEATURE [Sketcher::SketchObject] Sketch022
  FullyConstrained = true
  Placement = pos=(0,-14.3,2.37) rot=(-1,0,0;2.03453rad)
  sketch-geometry (6):
    g0: LineSegment StartX=41.65 StartY=-3.15 StartZ=0 EndX=38.95 EndY=-3.15 EndZ=0
    g1: LineSegment StartX=36.25 StartY=-3.15 StartZ=0 EndX=38.95 EndY=-3.15 EndZ=0
    g2: LineSegment StartX=41.65 StartY=-3.15 StartZ=0 EndX=41.65 EndY=-7.15 EndZ=0
    g3: LineSegment StartX=38.95 StartY=-7.15 StartZ=0 EndX=41.65 EndY=-7.15 EndZ=0
    g4: LineSegment StartX=38.95 StartY=-7.15 StartZ=0 EndX=36.25 EndY=-7.15 EndZ=0
    g5: LineSegment StartX=36.25 StartY=-3.15 StartZ=0 EndX=36.25 EndY=-7.15 EndZ=0
  constraints (16):
    c: Horizontal(g0)
    c: Distance(g0) = 2.7
    c: Horizontal(g1)
    c: Distance(g1) = 2.7
    c: Coincident(g1,g0)
    c: Block(g0)
    c: Coincident(g2,g0)
    c: Vertical(g2)
    c: Horizontal(g3)
    c: Coincident(g3,g2)
    c: Horizontal(g4)
    c: Coincident(g5,g1)
    c: Vertical(g5)
    c: Coincident(g5,g4)
    c: Block(g3)
    c: Block(g4)
FEATURE [Sketcher::SketchObject] Sketch024
  FullyConstrained = true
  Placement = pos=(0,-14.3,2.37) rot=(-1,0,0;2.03453rad)
  sketch-geometry (4):
    g0: LineSegment StartX=49.5 StartY=-21.2 StartZ=0 EndX=49.5 EndY=-22.8 EndZ=0
    g1: LineSegment StartX=49.5 StartY=-22.8 StartZ=0 EndX=0.002238 EndY=-22.8 EndZ=0
    g2: LineSegment StartX=0.002238 StartY=-21.2 StartZ=0 EndX=0.002238 EndY=-22.8 EndZ=0
    g3: LineSegment StartX=49.5 StartY=-21.2 StartZ=0 EndX=0.002238 EndY=-21.2 EndZ=0
  constraints (10):
    c: Vertical(g0)
    c: Distance(g0) = 1.6
    c: Coincident(g1,g0)
    c: Horizontal(g1)
    c: Vertical(g2)
    c: Coincident(g2,g1)
    c: Coincident(g3,g0)
    c: Coincident(g3,g2)
    c: Horizontal(g3)
    c: Block(g3)
FEATURE [Sketcher::SketchObject] Sketch025
  FullyConstrained = true
  Placement = pos=(0,-14.3,2.37) rot=(-1,0,0;2.03453rad)
  sketch-geometry (4):
    g0: LineSegment StartX=0 StartY=1.5 StartZ=0 EndX=0 EndY=0 EndZ=0
    g1: LineSegment StartX=0 StartY=1.5 StartZ=0 EndX=5 EndY=1.5 EndZ=0
    g2: LineSegment StartX=5 StartY=1.5 StartZ=0 EndX=5 EndY=0 EndZ=0
    g3: LineSegment StartX=0 StartY=0 StartZ=0 EndX=5 EndY=0 EndZ=0
  constraints (13):
    c: Vertical(g0)
    c: Distance(g0) = 1.5
    c: Horizontal(g1)
    c: Distance(g1) = 5
    c: Coincident(g1,g0)
    c: Vertical(g2)
    c: Distance(g2) = 1.5
    c: Coincident(g2,g1)
    c: Block(g1)
    c: Block(g2)
    c: Block(g0)
    c: Coincident(g3,g0)
    c: Coincident(g3,g2)
FEATURE [Part::Extrusion] Extrude022  label="solenoidDriverBottomLipTopExtrude014"
  Base = -> Sketch025
  Dir = (0,0.894389,-0.447291)
  DirMode = 2
  FaceMakerClass = Part::FaceMakerBullseye
  LengthFwd = -6.5
  LengthRev = 0
  Placement = pos=(0,-15.45,20.3) rot=(1,0,0;1.5708rad)
  Solid = true
  Symmetric = false
FEATURE [Part::Fillet] Fillet013  label="solenoidDriverBottomLipTopFillet006"
  Base = -> Extrude022
  Edges = 1 edges r=1.4: [Edge6]
  Placement = pos=(5,0,0) rot=(0,0,1;0rad)
FEATURE [Sketcher::SketchObject] Sketch026
  FullyConstrained = true
  Placement = pos=(0,-14.3,2.37) rot=(-1,0,0;2.03453rad)
  sketch-geometry (4):
    g0: LineSegment StartX=0 StartY=1.5 StartZ=0 EndX=0 EndY=0 EndZ=0
    g1: LineSegment StartX=0 StartY=1.5 StartZ=0 EndX=5 EndY=1.5 EndZ=0
    g2: LineSegment StartX=5 StartY=1.5 StartZ=0 EndX=5 EndY=0 EndZ=0
    g3: LineSegment StartX=0 StartY=0 StartZ=0 EndX=5 EndY=0 EndZ=0
  constraints (13):
    c: Vertical(g0)
    c: Distance(g0) = 1.5
    c: Horizontal(g1)
    c: Distance(g1) = 5
    c: Coincident(g1,g0)
    c: Vertical(g2)
    c: Distance(g2) = 1.5
    c: Coincident(g2,g1)
    c: Block(g1)
    c: Block(g2)
    c: Block(g0)
    c: Coincident(g3,g0)
    c: Coincident(g3,g2)
FEATURE [Part::Extrusion] Extrude023  label="solenoidDriverBottomLipTopExtrude015"
  Base = -> Sketch026
  Dir = (0,0.894389,-0.447291)
  DirMode = 2
  FaceMakerClass = Part::FaceMakerBullseye
  LengthFwd = -6.5
  LengthRev = 0
  Placement = pos=(5,-14.15,19.65) rot=(1,0,0;1.5708rad)
  Solid = true
  Symmetric = false
FEATURE [Sketcher::SketchObject] Sketch027
  FullyConstrained = true
  Placement = pos=(0,-14.3,2.37) rot=(-1,0,0;2.03453rad)
  sketch-geometry (5):
    g0: LineSegment StartX=45.5 StartY=-21.2 StartZ=0 EndX=49.5 EndY=-21.2 EndZ=0
    g1: LineSegment StartX=49.5 StartY=0 StartZ=0 EndX=49.5 EndY=-21.2 EndZ=0
    g2: LineSegment StartX=49.5 StartY=0 StartZ=0 EndX=49.5 EndY=1.6 EndZ=0
    g3: LineSegment StartX=45.5 StartY=-21.2 StartZ=0 EndX=45.5 EndY=1.6 EndZ=0
    g4: LineSegment StartX=49.5 StartY=1.6 StartZ=0 EndX=45.5 EndY=1.6 EndZ=0
  constraints (14):
    c: Horizontal(g0)
    c: Distance(g0) = 4
    c: Coincident(g1,g0)
    c: Vertical(g1)
    c: Block(g1)
    c: Vertical(g2)
    c: Distance(g2) = 1.6
    c: Block(g2)
    c: Coincident(g3,g0)
    c: Vertical(g3)
    c: Coincident(g4,g2)
    c: Horizontal(g4)
    c: Block(g0)
    c: Coincident(g3,g4)
FEATURE [Part::Extrusion] Extrude024
  Base = -> Sketch027
  Dir = (0,0.894389,-0.447291)
  DirMode = 2
  FaceMakerClass = Part::FaceMakerBullseye
  LengthFwd = 6.34
  LengthRev = 0
  Placement = pos=(0,-5.59,1) rot=(0,0,1;0rad)
  Solid = true
  Symmetric = false
FEATURE [Part::Fillet] Fillet014  label="solenoidDriverSideBarFillet014"
  Base = -> Extrude024
  Edges = 1 edges r=1.4: [Edge14]
  Placement = pos=(0,0.9,-0.45) rot=(0,0,1;0rad)
FEATURE [Part::Revolution] Revolve  label="mainScrewStandRevolve"
  Angle = 360
  Axis = (0,0,1)
  Base = (0,0,0)
  FaceMakerClass = Part::FaceMakerBullseye
  Placement = pos=(121.35,-15.3,0) rot=(0,0,1;0rad)
  Solid = true
  Source = -> Sketch004
  Symmetric = false
FEATURE [Part::Extrusion] Extrude021  label="solenoidDriverTopLipLowerExtrude011"
  Base = -> Sketch024
  Dir = (0,0.894389,-0.447291)
  DirMode = 2
  FaceMakerClass = Part::FaceMakerBullseye
  LengthFwd = 5.05
  LengthRev = 0
  Solid = true
  Symmetric = false
FEATURE [Part::Fillet] Fillet012  label="solenoidDriverTopLipLowerFillet004"
  Base = -> Extrude021
  Edges = 1 edges r=1.2: [Edge7]
  Placement = pos=(0,-0.9,-1.35) rot=(0,0,1;0rad)
FEATURE [Part::Fillet] Fillet003  label="solenoidDriverTopLipLowerFillet003"
  Base = -> Extrude010
  Edges = 1 edges r=1.2: [Edge7]
  Placement = pos=(0,-3,-0.3) rot=(0,0,1;0rad)
FEATURE [Part::Extrusion] Extrude025  label="mainBodyUpperExtrude025"
  Base = -> Sketch001
  Dir = (0,0,1)
  DirMode = 2
  FaceMakerClass = Part::FaceMakerBullseye
  LengthFwd = 20
  LengthRev = 0
  Solid = true
  Symmetric = false
FEATURE [Part::MultiFuse] Fusion  label="solenoidDriverBottomLipFusion"
  Placement = pos=(0,-1.6,0) rot=(0,0,1;0rad)
  Shapes = -> [Fillet005,Fillet013,Extrude023,Extrude013]
FEATURE [Sketcher::SketchObject] Sketch028
  FullyConstrained = true
  Placement = pos=(0,-14.3,2.37) rot=(-1,0,0;2.03453rad)
  sketch-geometry (4):
    g0: LineSegment StartX=0 StartY=1.5 StartZ=0 EndX=0 EndY=0 EndZ=0
    g1: LineSegment StartX=0 StartY=1.5 StartZ=0 EndX=5 EndY=1.5 EndZ=0
    g2: LineSegment StartX=5 StartY=1.5 StartZ=0 EndX=5 EndY=0 EndZ=0
    g3: LineSegment StartX=0 StartY=0 StartZ=0 EndX=5 EndY=0 EndZ=0
  constraints (13):
    c: Vertical(g0)
    c: Distance(g0) = 1.5
    c: Horizontal(g1)
    c: Distance(g1) = 5
    c: Coincident(g1,g0)
    c: Vertical(g2)
    c: Distance(g2) = 1.5
    c: Coincident(g2,g1)
    c: Block(g1)
    c: Block(g2)
    c: Block(g0)
    c: Coincident(g3,g0)
    c: Coincident(g3,g2)
FEATURE [Part::Extrusion] Extrude026  label="solenoidDriverBottomLipTopExtrude016"
  Base = -> Sketch028
  Dir = (0,0.894389,-0.447291)
  DirMode = 2
  FaceMakerClass = Part::FaceMakerBullseye
  LengthFwd = -6.5
  LengthRev = 0
  Placement = pos=(5,-14.15,19.65) rot=(1,0,0;1.5708rad)
  Solid = true
  Symmetric = false
FEATURE [Sketcher::SketchObject] Sketch029
  FullyConstrained = true
  Placement = pos=(0,-14.3,2.37) rot=(-1,0,0;2.03453rad)
  sketch-geometry (4):
    g0: LineSegment StartX=0 StartY=1.5 StartZ=0 EndX=0 EndY=0 EndZ=0
    g1: LineSegment StartX=0 StartY=1.5 StartZ=0 EndX=5 EndY=1.5 EndZ=0
    g2: LineSegment StartX=5 StartY=1.5 StartZ=0 EndX=5 EndY=0 EndZ=0
    g3: LineSegment StartX=0 StartY=0 StartZ=0 EndX=5 EndY=0 EndZ=0
  constraints (13):
    c: Vertical(g0)
    c: Distance(g0) = 1.5
    c: Horizontal(g1)
    c: Distance(g1) = 5
    c: Coincident(g1,g0)
    c: Vertical(g2)
    c: Distance(g2) = 1.5
    c: Coincident(g2,g1)
    c: Block(g1)
    c: Block(g2)
    c: Block(g0)
    c: Coincident(g3,g0)
    c: Coincident(g3,g2)
FEATURE [Part::Extrusion] Extrude027  label="solenoidDriverBottomLipTopExtrude017"
  Base = -> Sketch029
  Dir = (0,0.894389,-0.447291)
  DirMode = 2
  FaceMakerClass = Part::FaceMakerBullseye
  LengthFwd = -6.5
  LengthRev = 0
  Placement = pos=(0,-14.15,19.65) rot=(1,0,0;1.5708rad)
  Solid = true
  Symmetric = false
FEATURE [Sketcher::SketchObject] Sketch030
  FullyConstrained = true
  Placement = pos=(0,-14.3,2.37) rot=(-1,0,0;2.03453rad)
  sketch-geometry (4):
    g0: LineSegment StartX=0 StartY=1.5 StartZ=0 EndX=0 EndY=0 EndZ=0
    g1: LineSegment StartX=0 StartY=1.5 StartZ=0 EndX=5 EndY=1.5 EndZ=0
    g2: LineSegment StartX=5 StartY=1.5 StartZ=0 EndX=5 EndY=0 EndZ=0
    g3: LineSegment StartX=0 StartY=0 StartZ=0 EndX=5 EndY=0 EndZ=0
  constraints (13):
    c: Vertical(g0)
    c: Distance(g0) = 1.5
    c: Horizontal(g1)
    c: Distance(g1) = 5
    c: Coincident(g1,g0)
    c: Vertical(g2)
    c: Distance(g2) = 1.5
    c: Coincident(g2,g1)
    c: Block(g1)
    c: Block(g2)
    c: Block(g0)
    c: Coincident(g3,g0)
    c: Coincident(g3,g2)
FEATURE [Sketcher::SketchObject] Sketch031
  FullyConstrained = true
  Placement = pos=(0,-14.3,2.37) rot=(-1,0,0;2.03453rad)
  sketch-geometry (6):
    g0: LineSegment StartX=45.5 StartY=-21.2 StartZ=0 EndX=49.5 EndY=-21.2 EndZ=0
    g1: LineSegment StartX=45.5 StartY=0 StartZ=0 EndX=49.5 EndY=0 EndZ=0
    g2: LineSegment StartX=49.5 StartY=0 StartZ=0 EndX=49.5 EndY=-21.2 EndZ=0
    g3: LineSegment StartX=4 StartY=0 StartZ=0 EndX=4 EndY=-21.2 EndZ=0
    g4: LineSegment StartX=45.5 StartY=-21.2 StartZ=0 EndX=4 EndY=-21.2 EndZ=0
    g5: LineSegment StartX=4 StartY=0 StartZ=0 EndX=45.5 EndY=0 EndZ=0
  constraints (16):
    c: Horizontal(g0)
    c: Distance(g0) = 4
    c: Horizontal(g1)
    c: Distance(g1) = 4
    c: Coincident(g2,g1)
    c: Coincident(g2,g0)
    c: Vertical(g2)
    c: Block(g2)
    c: Vertical(g3)
    c: Coincident(g4,g0)
    c: Horizontal(g4)
    c: Coincident(g4,g3)
    c: Coincident(g5,g1)
    c: Horizontal(g5)
    c: Block(g3)
    c: Block(g5)
FEATURE [Part::Extrusion] Extrude028  label="removeFromSolenoidDriverMainExtrude021"
  Base = -> Sketch031
  Dir = (0,0.894389,-0.447291)
  DirMode = 2
  FaceMakerClass = Part::FaceMakerBullseye
  LengthFwd = 3.1
  LengthRev = 0
  Placement = pos=(-4,-2.42,-0.8) rot=(0,0,1;0rad)
  Solid = true
  Symmetric = false
FEATURE [Part::Extrusion] Extrude029  label="solenoidDriverBottomLipTopExtrude018"
  Base = -> Sketch030
  Dir = (0,0.894389,-0.447291)
  DirMode = 2
  FaceMakerClass = Part::FaceMakerBullseye
  LengthFwd = -6.5
  LengthRev = 0
  Placement = pos=(5,-14.15,19.65) rot=(1,0,0;1.5708rad)
  Solid = true
  Symmetric = false
FEATURE [Sketcher::SketchObject] Sketch032
  FullyConstrained = true
  Placement = pos=(0,-14.3,2.37) rot=(-1,0,0;2.03453rad)
  sketch-geometry (4):
    g0: LineSegment StartX=0 StartY=1.5 StartZ=0 EndX=0 EndY=0 EndZ=0
    g1: LineSegment StartX=0 StartY=1.5 StartZ=0 EndX=5 EndY=1.5 EndZ=0
    g2: LineSegment StartX=5 StartY=1.5 StartZ=0 EndX=5 EndY=0 EndZ=0
    g3: LineSegment StartX=0 StartY=0 StartZ=0 EndX=5 EndY=0 EndZ=0
  constraints (13):
    c: Vertical(g0)
    c: Distance(g0) = 1.5
    c: Horizontal(g1)
    c: Distance(g1) = 5
    c: Coincident(g1,g0)
    c: Vertical(g2)
    c: Distance(g2) = 1.5
    c: Coincident(g2,g1)
    c: Block(g1)
    c: Block(g2)
    c: Block(g0)
    c: Coincident(g3,g0)
    c: Coincident(g3,g2)
FEATURE [Part::Extrusion] Extrude030  label="solenoidDriverBottomLipTopExtrude019"
  Base = -> Sketch032
  Dir = (0,0.894389,-0.447291)
  DirMode = 2
  FaceMakerClass = Part::FaceMakerBullseye
  LengthFwd = -6.5
  LengthRev = 0
  Placement = pos=(0,-14.15,19.65) rot=(1,0,0;1.5708rad)
  Solid = true
  Symmetric = false
FEATURE [Part::MultiFuse] Fusion004
  Placement = pos=(0,1.4,2.65) rot=(0,0,1;0rad)
  Shapes = -> [Extrude029,Extrude030]
FEATURE [Part::MultiFuse] Fusion003
  Placement = pos=(-2.3,0,0) rot=(0,0,1;0rad)
  Shapes = -> [Extrude028,Fusion004]
FEATURE [Sketcher::SketchObject] Sketch033
  FullyConstrained = true
  Placement = pos=(0,-14.3,2.37) rot=(-1,0,0;2.03453rad)
  sketch-geometry (4):
    g0: LineSegment StartX=0 StartY=1.5 StartZ=0 EndX=0 EndY=0 EndZ=0
    g1: LineSegment StartX=0 StartY=1.5 StartZ=0 EndX=5 EndY=1.5 EndZ=0
    g2: LineSegment StartX=5 StartY=1.5 StartZ=0 EndX=5 EndY=0 EndZ=0
    g3: LineSegment StartX=0 StartY=0 StartZ=0 EndX=5 EndY=0 EndZ=0
  constraints (13):
    c: Vertical(g0)
    c: Distance(g0) = 1.5
    c: Horizontal(g1)
    c: Distance(g1) = 5
    c: Coincident(g1,g0)
    c: Vertical(g2)
    c: Distance(g2) = 1.5
    c: Coincident(g2,g1)
    c: Block(g1)
    c: Block(g2)
    c: Block(g0)
    c: Coincident(g3,g0)
    c: Coincident(g3,g2)
FEATURE [Sketcher::SketchObject] Sketch034
  FullyConstrained = true
  Placement = pos=(0,-14.3,2.37) rot=(-1,0,0;2.03453rad)
  sketch-geometry (4):
    g0: LineSegment StartX=0 StartY=1.5 StartZ=0 EndX=0 EndY=0 EndZ=0
    g1: LineSegment StartX=0 StartY=1.5 StartZ=0 EndX=5 EndY=1.5 EndZ=0
    g2: LineSegment StartX=5 StartY=1.5 StartZ=0 EndX=5 EndY=0 EndZ=0
    g3: LineSegment StartX=0 StartY=0 StartZ=0 EndX=5 EndY=0 EndZ=0
  constraints (13):
    c: Vertical(g0)
    c: Distance(g0) = 1.5
    c: Horizontal(g1)
    c: Distance(g1) = 5
    c: Coincident(g1,g0)
    c: Vertical(g2)
    c: Distance(g2) = 1.5
    c: Coincident(g2,g1)
    c: Block(g1)
    c: Block(g2)
    c: Block(g0)
    c: Coincident(g3,g0)
    c: Coincident(g3,g2)
FEATURE [Part::Extrusion] Extrude020  label="removeFromSolenoidDriverMainExtrude020"
  Base = -> Sketch020
  Dir = (0,0.894389,-0.447291)
  DirMode = 2
  FaceMakerClass = Part::FaceMakerBullseye
  LengthFwd = 3.1
  LengthRev = 0
  Placement = pos=(-4,-2.42,-0.8) rot=(0,0,1;0rad)
  Solid = true
  Symmetric = false
FEATURE [Part::Fillet] Fillet
  Base = -> Fusion003
  Edges = 1 edges r=10: [Edge5]
  Placement = pos=(-2,0,0) rot=(0,0,1;0rad)
FEATURE [Part::MultiFuse] Fusion001
  Placement = pos=(0,1.4,2.65) rot=(0,0,1;0rad)
  Shapes = -> [Extrude026,Extrude027]
FEATURE [Part::MultiFuse] Fusion002
  Shapes = -> [Extrude020,Fusion001]
FEATURE [Sketcher::SketchObject] Sketch035
  FullyConstrained = true
  Placement = pos=(0,-14.3,2.37) rot=(-1,0,0;2.03453rad)
  sketch-geometry (4):
    g0: LineSegment StartX=0 StartY=1.5 StartZ=0 EndX=0 EndY=0 EndZ=0
    g1: LineSegment StartX=0 StartY=1.5 StartZ=0 EndX=5 EndY=1.5 EndZ=0
    g2: LineSegment StartX=5 StartY=1.5 StartZ=0 EndX=5 EndY=0 EndZ=0
    g3: LineSegment StartX=0 StartY=0 StartZ=0 EndX=5 EndY=0 EndZ=0
  constraints (13):
    c: Vertical(g0)
    c: Distance(g0) = 1.5
    c: Horizontal(g1)
    c: Distance(g1) = 5
    c: Coincident(g1,g0)
    c: Vertical(g2)
    c: Distance(g2) = 1.5
    c: Coincident(g2,g1)
    c: Block(g1)
    c: Block(g2)
    c: Block(g0)
    c: Coincident(g3,g0)
    c: Coincident(g3,g2)
FEATURE [Sketcher::SketchObject] Sketch036
  FullyConstrained = true
  Placement = pos=(0,-14.3,2.37) rot=(-1,0,0;2.03453rad)
  sketch-geometry (4):
    g0: LineSegment StartX=0 StartY=1.5 StartZ=0 EndX=0 EndY=0 EndZ=0
    g1: LineSegment StartX=0 StartY=1.5 StartZ=0 EndX=5 EndY=1.5 EndZ=0
    g2: LineSegment StartX=5 StartY=1.5 StartZ=0 EndX=5 EndY=0 EndZ=0
    g3: LineSegment StartX=0 StartY=0 StartZ=0 EndX=5 EndY=0 EndZ=0
  constraints (13):
    c: Vertical(g0)
    c: Distance(g0) = 1.5
    c: Horizontal(g1)
    c: Distance(g1) = 5
    c: Coincident(g1,g0)
    c: Vertical(g2)
    c: Distance(g2) = 1.5
    c: Coincident(g2,g1)
    c: Block(g1)
    c: Block(g2)
    c: Block(g0)
    c: Coincident(g3,g0)
    c: Coincident(g3,g2)
FEATURE [Part::Extrusion] Extrude031  label="solenoidDriverBottomLipTopExtrude020"
  Base = -> Sketch035
  Dir = (0,0.894389,-0.447291)
  DirMode = 2
  FaceMakerClass = Part::FaceMakerBullseye
  LengthFwd = -6.5
  LengthRev = 0
  Placement = pos=(5,-14.15,19.65) rot=(1,0,0;1.5708rad)
  Solid = true
  Symmetric = false
FEATURE [Part::Extrusion] Extrude032  label="solenoidDriverBottomLipTopExtrude021"
  Base = -> Sketch036
  Dir = (0,0.894389,-0.447291)
  DirMode = 2
  FaceMakerClass = Part::FaceMakerBullseye
  LengthFwd = -6.5
  LengthRev = 0
  Placement = pos=(0,-14.15,19.65) rot=(1,0,0;1.5708rad)
  Solid = true
  Symmetric = false
FEATURE [Part::MultiFuse] Fusion009
  Placement = pos=(8,1.4,2.65) rot=(0,0,1;0rad)
  Shapes = -> [Extrude031,Extrude032]
FEATURE [Part::MultiFuse] Fusion010  label="removeFromSolenoidDriver"
  Shapes = -> [Fusion009,Fillet,Fusion002]
FEATURE [Sketcher::SketchObject] Sketch037
  FullyConstrained = true
  Placement = pos=(0,0,0) rot=(1,0,0;1.5708rad)
  sketch-geometry (4):
    g0: Circle CenterX=64.05 CenterY=16.5 CenterZ=0 NormalX=0 NormalY=0 NormalZ=1 AngleXU=0 Radius=2.7
    g1: Circle CenterX=64.05 CenterY=8.5 CenterZ=0 NormalX=0 NormalY=0 NormalZ=1 AngleXU=0 Radius=2.7
    g2: Circle CenterX=84.15 CenterY=8.5 CenterZ=0 NormalX=0 NormalY=0 NormalZ=1 AngleXU=0 Radius=2.7
    g3: Circle CenterX=84.15 CenterY=16.5 CenterZ=0 NormalX=0 NormalY=0 NormalZ=1 AngleXU=0 Radius=2.7
  constraints (4):
    c: Block(g2)
    c: Block(g3)
    c: Block(g0)
    c: Block(g1)
FEATURE [Part::Extrusion] Extrude033  label="removeFromMainBodyToCreateScrewHoleCounterSinks001"
  Base = -> Sketch037
  Dir = (0,-1,1.1e-15)
  DirMode = 2
  FaceMakerClass = Part::FaceMakerBullseye
  LengthFwd = 1.9
  LengthRev = 0
  Placement = pos=(0.8,0,0) rot=(0,0,1;0rad)
  Solid = true
  Symmetric = false
FEATURE [Part::MultiFuse] Fusion011  label="removeFromMainBodyToCreateScrewHoleCounterSinks001Fusion011"
  Shapes = -> [Extrude014,Extrude033]
FEATURE [Sketcher::SketchObject] Sketch038
  FullyConstrained = true
  Placement = pos=(0,-14.3,2.37) rot=(-1,0,0;2.03453rad)
  sketch-geometry (4):
    g0: LineSegment StartX=33.9 StartY=-9.7 StartZ=0 EndX=33.9 EndY=-1.5 EndZ=0
    g1: LineSegment StartX=33.9 StartY=-1.5 StartZ=0 EndX=44.5 EndY=-1.5 EndZ=0
    g2: LineSegment StartX=33.9 StartY=-9.7 StartZ=0 EndX=44.5 EndY=-9.7 EndZ=0
    g3: LineSegment StartX=44.5 StartY=-1.5 StartZ=0 EndX=44.5 EndY=-9.7 EndZ=0
  constraints (10):
    c: Vertical(g0)
    c: Coincident(g1,g0)
    c: Horizontal(g1)
    c: Block(g1)
    c: Block(g0)
    c: Coincident(g2,g0)
    c: Horizontal(g2)
    c: Coincident(g3,g1)
    c: Coincident(g3,g2)
    c: Vertical(g3)
FEATURE [Part::Extrusion] Extrude034
  Base = -> Sketch038
  Dir = (0,0.894389,-0.447291)
  DirMode = 2
  FaceMakerClass = Part::FaceMakerBullseye
  LengthFwd = 16
  LengthRev = 0
  Placement = pos=(0,-22,7) rot=(0,0,1;0rad)
  Solid = true
  Symmetric = false
FEATURE [Sketcher::SketchObject] Sketch039
  FullyConstrained = true
  Placement = pos=(0,-14.3,2.37) rot=(-1,0,0;2.03453rad)
  sketch-geometry (4):
    g0: LineSegment StartX=5.5 StartY=-7.7 StartZ=0 EndX=13.3 EndY=-7.7 EndZ=0
    g1: LineSegment StartX=13.3 StartY=-7.7 StartZ=0 EndX=13.3 EndY=-13.1 EndZ=0
    g2: LineSegment StartX=13.3 StartY=-13.1 StartZ=0 EndX=5.5 EndY=-13.1 EndZ=0
    g3: LineSegment StartX=5.5 StartY=-7.7 StartZ=0 EndX=5.5 EndY=-13.1 EndZ=0
  constraints (12):
    c: Horizontal(g0)
    c: Distance(g0) = 7.8
    c: Coincident(g1,g0)
    c: Vertical(g1)
    c: Distance(g1) = 5.4
    c: Coincident(g2,g1)
    c: Horizontal(g2)
    c: Vertical(g3)
    c: Coincident(g3,g2)
    c: Block(g0)
    c: Block(g2)
    c: Block(g3)
FEATURE [Part::Extrusion] Extrude035  label="removeToMakeHoleForConnectorExtrude035"
  Base = -> Sketch039
  Dir = (0,0.894389,-0.447291)
  DirMode = 2
  FaceMakerClass = Part::FaceMakerBullseye
  LengthFwd = 15
  LengthRev = 0
  Placement = pos=(-4,-22,9.6469) rot=(0,0,1;0rad)
  Solid = true
  Symmetric = false
FEATURE [App::MeasureDistance] Distance  label="Distance: 4.00 mm"
  Distance = 4.00184
  P1 = (119.349,-15.3,8)
  P2 = (123.351,-15.3,8)
FEATURE [App::MeasureDistance] Distance001  label="Distance: 3.80 mm"
  Distance = 3.8
  P1 = (119.45,-15.3,8)
  P2 = (123.25,-15.3,8)
FEATURE [Part::Fillet] Fillet015
  Base = -> Extrude009
  Edges = 1 edges r=1.59: [Edge7]
FEATURE [Part::Fillet] Fillet016
  Base = -> Extrude017
  Edges = 1 edges r=1.49: [Edge12]
FEATURE [Part::Fillet] Fillet017
  Base = -> Fillet016
  Edges = 1 edges r=1.45: [Edge8]
FEATURE [Part::MultiFuse] Fusion012  label="main"
  Shapes = -> [Extrude,Revolve,Extrude005,Fillet003,Fillet012,Fillet014,Extrude025,Fusion,Fillet015,Fillet017]
FEATURE [Part::Cut] Cut001
  Base = -> Fusion012
  Tool = -> Box003
FEATURE [Part::Cut] Cut002
  Base = -> Cut001
  Tool = -> Box002
FEATURE [Part::Cut] Cut003
  Base = -> Cut002
  Tool = -> Cut
FEATURE [Part::Cut] Cut004
  Base = -> Cut003
  Tool = -> Extrude019
FEATURE [Part::Cut] Cut005
  Base = -> Cut004
  Tool = -> Fusion011
FEATURE [Part::Cut] Cut006
  Base = -> Cut005
  Tool = -> Extrude004
FEATURE [Part::Cut] Cut007
  Base = -> Cut006
  Tool = -> Extrude015
FEATURE [Part::Cut] Cut008
  Base = -> Cut007
  Tool = -> Extrude008
FEATURE [Part::Cut] Cut009
  Base = -> Cut008
  Tool = -> Fusion010
FEATURE [App::MeasureDistance] Distance002  label="Distance: 2.05 mm"
  Distance = 2.05453
  P1 = (1.5,-23.0732,21.402)
  P2 = (6e-15,-23,20)
FEATURE [Part::Cut] Cut010
  Base = -> Cut009
  Tool = -> Extrude035
FEATURE [Part::Cut] Cut011
  Base = -> Cut010
  Tool = -> Extrude034
FEATURE [Part::Fillet] Fillet018
  Base = -> Cut011
  Edges = 1 edges r=3: [Edge134]
FEATURE [Part::Fillet] Fillet019
  Base = -> Fillet018
  Edges = 1 edges r=3: [Edge29]
FEATURE [Part::Box] Box004  label="Cube004"
  AttacherType = Attacher::AttachEngine3D
  Height = 10
  Length = 200
  Placement = pos=(-30,0,0) rot=(0,0,1;0rad)
  Width = 10
FEATURE [Part::Fillet] Fillet020
  Base = -> Box004
  Edges = 1 edges r=3.6: [Edge12]
FEATURE [Part::Box] Box005  label="Cube005"
  AttacherType = Attacher::AttachEngine3D
  Height = 10
  Length = 198
  Placement = pos=(-30,0,0) rot=(0,0,1;0rad)
  Width = 10
FEATURE [Part::Cut] Cut012
  Base = -> Box005
  Tool = -> Fillet020
FEATURE [Part::Box] Box006  label="Cube006"
  AttacherType = Attacher::AttachEngine3D
  Height = 5
  Length = 200
  Placement = pos=(-30,6.4,10) rot=(1,0,0;0rad)
  Width = 5
FEATURE [Part::Box] Box007  label="Cube007"
  AttacherType = Attacher::AttachEngine3D
  Height = 5
  Length = 200
  Placement = pos=(-30,6.4,10) rot=(1,0,0;0.872665rad)
  Width = 5
FEATURE [Part::MultiFuse] Fusion013  label="removeFromMainFusion013"
  Placement = pos=(0,-10,10) rot=(0,0,1;0rad)
  Shapes = -> [Box007,Box006,Cut012]
FEATURE [Part::Cut] Cut013
  Base = -> Fillet019
  Tool = -> Fusion013
FEATURE [Mesh::Feature] v0_98_Cut013  label="v0_98-Cut013"
FEATURE [App::MeasureDistance] Distance003  label="Distance: 7.18 mm"
  Distance = 7.17719
  P1 = (117.773,-15.3145,-2.4)
  P2 = (124.951,-15.2973,-2.4)
